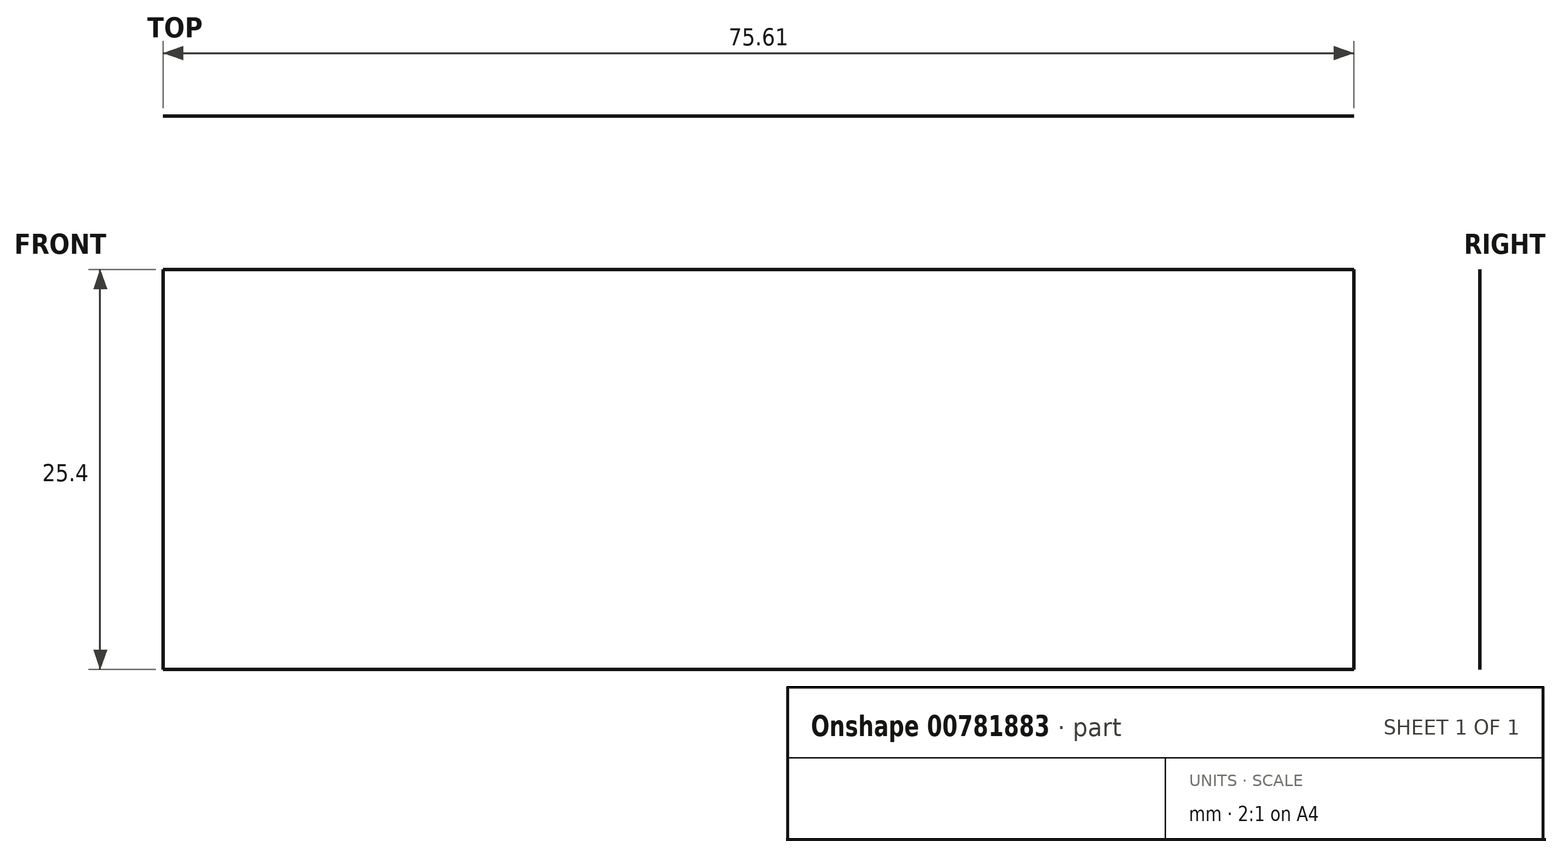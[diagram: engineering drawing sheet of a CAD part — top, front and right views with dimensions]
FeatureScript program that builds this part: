
annotation { "Feature Type Name" : "Feature", "Feature Type Description" : "" }
export const myFeature = defineFeature(function(context is Context, id is Id, definition is map)
    precondition{}
    {
        {
            var Q0;
            Q0=qCreatedBy(makeId("Top.planeOp"),FACE);
            var sketch = newSketch(context, id + "F0", { "sketchPlane" : qUnion([Q0])});
            skLineSegment(sketch, "E0.bottom", {"start": v(0, 0) * mm, "end": v(75.61, 0) * mm});
            skLineSegment(sketch, "E0.top", {"start": v(0, 32.75) * mm, "end": v(75.61, 32.75) * mm});
            skLineSegment(sketch, "E0.left", {"start": v(0, 0) * mm, "end": v(0, 32.75) * mm});
            skLineSegment(sketch, "E0.right", {"start": v(75.61, 0) * mm, "end": v(75.61, 32.75) * mm});
            skSolve(sketch);
        }
        {
            var Q0;
            Q0=sQuery(id+"F0.wireOp",EDGE,"E0.top");
            extrude(context, id + "F1", {"bodyType" : ToolBodyType.SURFACE, "surfaceEntities" : qUnion([Q0]), "depth" : 25.4 * mm, "offsetDistance" : 25.4 * mm});
        }
    });
